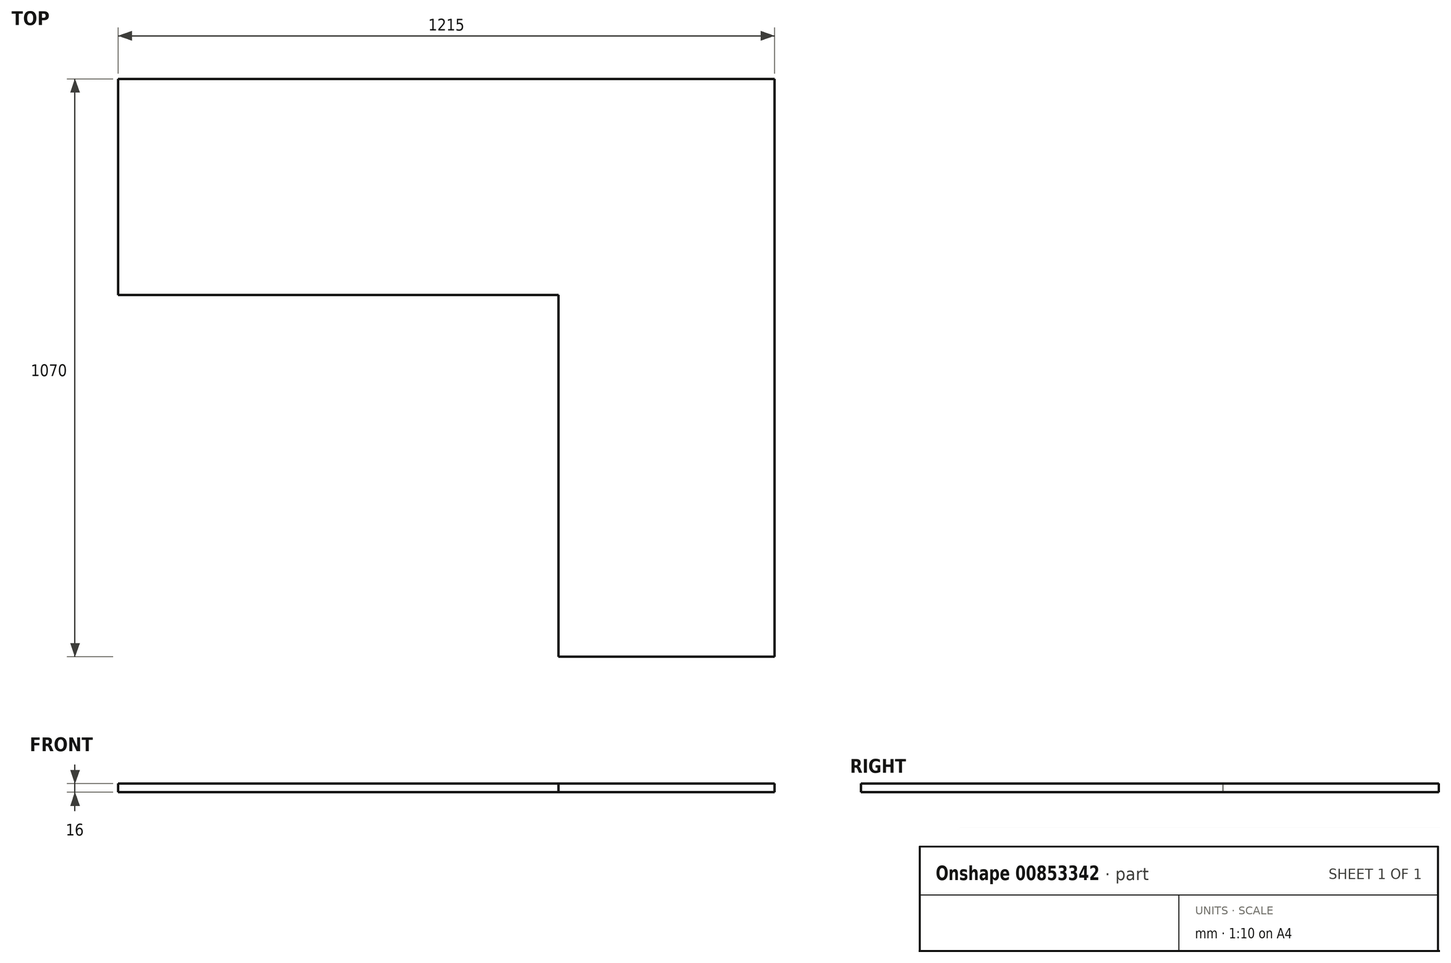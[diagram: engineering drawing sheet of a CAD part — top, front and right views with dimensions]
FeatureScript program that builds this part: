
annotation { "Feature Type Name" : "Feature", "Feature Type Description" : "" }
export const myFeature = defineFeature(function(context is Context, id is Id, definition is map)
    precondition{}
    {
        {
            var Q0;
            Q0=qCreatedBy(makeId("Top.planeOp"),FACE);
            var sketch = newSketch(context, id + "F0", { "sketchPlane" : qUnion([Q0])});
            skLineSegment(sketch, "E0", {"start": v(-1317.76, 0) * mm, "end": v(-102.76, 0) * mm});
            skLineSegment(sketch, "E1", {"start": v(-102.76, 0) * mm, "end": v(-102.76, -1070) * mm});
            skLineSegment(sketch, "E2", {"start": v(-102.76, -1070) * mm, "end": v(-502.76, -1070) * mm});
            skLineSegment(sketch, "E3", {"start": v(-502.76, -1070) * mm, "end": v(-502.76, -400) * mm});
            skLineSegment(sketch, "E4", {"start": v(-1317.76, 0) * mm, "end": v(-1317.76, -400) * mm});
            skLineSegment(sketch, "E5", {"start": v(-1317.76, -400) * mm, "end": v(-502.76, -400) * mm});
            skSolve(sketch);
        }
        {
            var Q0;
            Q0 = qSketchRegion(id + "F0", true);
            extrude(context, id + "F1", {"entities" : qUnion([Q0]), "depth" : 16 * mm, "offsetDistance" : 25 * mm});
        }
    });
